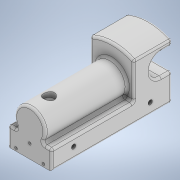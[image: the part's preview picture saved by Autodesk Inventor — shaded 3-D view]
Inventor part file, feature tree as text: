
AUTODESK INVENTOR PART (.ipt)
format: ipt  version: 2020 (Build 240168000, 168)  size: 304,640 bytes
history: native  units: in
note: dims shown in document units (in); Inventor stores cm internally (conversion verified against a paired STEP export)
features: sketch x9, extrude x8, hole x1, plane x1, fillet x1
ambient origin geometry x8: Origin, YZ Plane, XZ Plane, XY Plane, X Axis, Y Axis, Z Axis, Center Point
bodies: Solid1 (feature_tree)
feature tree (20):
  extrude  "Extrusion1"  Depth=5.5in
  extrude  "Extrusion2"  Depth=2.0in TaperAngle=0.0deg
  extrude  "Extrusion3"  Depth=2.0in TaperAngle=0.0deg
  extrude  "Extrusion4"  Depth=2.0in TaperAngle=0.0deg
  extrude  "Extrusion5"  Depth=0.5in
  hole  "Hole1"  [1 undecoded]
  extrude  "Extrusion6"  Depth=2.325in
  extrude  "Extrusion7"  Depth=1.0in
  plane  "Work Plane1"
  extrude  "Extrusion8"  Depth=0.5in
  fillet  "Fillet2"  Radius=0.5in
  sketch  "Sketch3"  dims[d1=0.875in d2=5.5in]
  sketch  "Sketch4"  dims[d3=1.75in d4=2.0in d5=0.0in]
  sketch  "Sketch5"  dims[d6=1.375in d7=2.0in d8=0.0in]
  sketch  "Sketch6"  dims[d9=3.0in d10=2.0in d11=0.0in]
  sketch  "Sketch7"  dims[d12=1.0in d13=0.5in]
  sketch  "Sketch8"  dims[d14=1.75in d15=2.0in d16=0.0in]
  sketch  "Sketch9"  dims[d17=0.25in d18=2.325in]
  sketch  "Sketch10"  dims[d19=2.0in d20=0.0in d21=1.0in]
  sketch  "Sketch11"  dims[d22=4.5in d23=0.5in d24=0.5in d25=0.196in d26=0.5in d27=0.375in d28=0.25in d29=0.5635in d30=0.75in d31=0.8108in d32=0.125in d33=0.125in d34=0.125in d35=0.375in d37=1.0in d38=1.625in d39=0.125in d40=0.125in d41=0.625in d42=0.125in d43=0.0in d44=0.25in d45=0.375in d46=1.0in d47=0.5in d48=0.0in d49=0.5in d50=0.875in d51=0.25in d52=0.0in d54=0.1in d53=0.5in]
note: 1 required parameter value undecoded (feature->parameter linkage not recoverable at this tier; creation-order binding heuristic only, values carry confidence <= 0.55)
